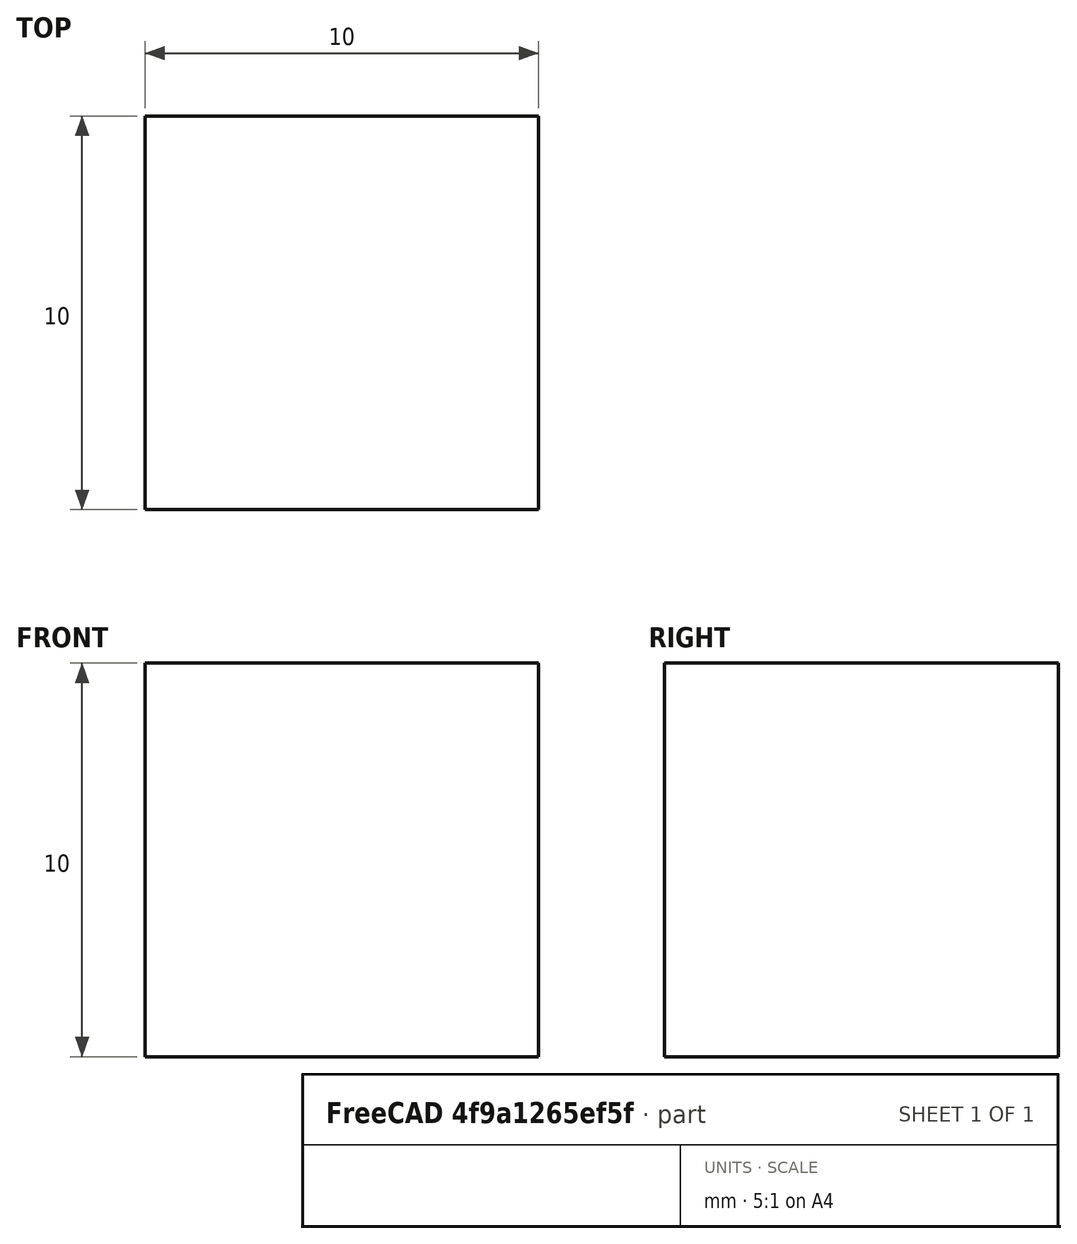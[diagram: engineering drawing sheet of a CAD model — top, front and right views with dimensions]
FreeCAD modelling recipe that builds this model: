
FCSTD DOCUMENT  (FreeCAD 0.21R33694 (Git))
Label: Block_Disp_Control_Example
License: All rights reserved
LicenseURL: http://en.wikipedia.org/wiki/All_rights_reserved
objects: Fem::ConstraintDisplacement×4, Fem::FemMeshObjectPython×2, Part::Box×1, Fem::FemSolverObjectPython×1, App::MaterialObjectPython×1, Fem::FemResultObjectPython×1, Fem::FemAnalysis×1
note: 1 computed B-rep shape members (.brp) not serialized (recipe doc carries the construction recipe, not evaluated geometry)

FEATURE [Part::Box] Box  label="Cube"
  AttacherType = Attacher::AttachEngine3D
  Height = 10
  Length = 10
  MapMode = 0
  Width = 10
FEATURE [Fem::FemSolverObjectPython] SolverCcxTools  # WARN: FeaturePython — macro-defined, semantics opaque (R4)
  AnalysisType = 0
  BeamShellResultOutput3D = false
  BucklingFactors = 1
  EigenmodeHighLimit = 1000000
  EigenmodeLowLimit = 0
  EigenmodesCount = 10
  GeometricalNonlinearity = 0
  IterationsControlParameterCutb = 0.25,0.5,0.75,0.85,,,1.5,
  IterationsControlParameterIter = 4,8,9,200,10,400,,200,,
  IterationsControlParameterTimeUse = false
  IterationsThermoMechMaximum = 2000
  IterationsUserDefinedIncrementations = false
  IterationsUserDefinedTimeStepLength = false
  MaterialNonlinearity = 0
  MatrixSolverType = 0
  SplitInputWriter = false
  ThermoMechSteadyState = true
  TimeEnd = 1
  TimeInitialStep = 0.01
FEATURE [App::MaterialObjectPython] MaterialSolid  # WARN: FeaturePython — macro-defined, semantics opaque (R4)
  Category = 0
FEATURE [Fem::FemMeshObjectPython] FEMMeshGmsh  # WARN: FeaturePython — macro-defined, semantics opaque (R4)
  Algorithm2D = 0
  Algorithm3D = 0
  CharacteristicLengthMax = 0
  CharacteristicLengthMin = 10
  CoherenceMesh = true
  ElementDimension = 0
  ElementOrder = 1
  GeometryTolerance = 1e-06
  GroupsOfNodes = false
  HighOrderOptimize = 0
  MeshSizeFromCurvature = 12
  OptimizeNetgen = false
  OptimizeStd = true
  Part = -> Box
  RecombinationAlgorithm = 0
  Recombine3DAll = false
  RecombineAll = false
  SecondOrderLinear = false
FEATURE [Fem::ConstraintDisplacement] ConstraintDisplacement
  NormalDirection = (0,0,-1)
  References = -> [Box]
  Scale = 1
  hasXFormula = false
  hasYFormula = false
  hasZFormula = false
  rotxFix = false
  rotxFree = true
  rotyFix = false
  rotyFree = true
  rotzFix = false
  rotzFree = true
  useFlowSurfaceForce = false
  xDisplacement = 0
  xFix = false
  xFree = true
  xRotation = 0
  yDisplacement = 0
  yFix = false
  yFree = true
  yRotation = 0
  zDisplacement = 0
  zFix = false
  zFree = false
  zRotation = 0
FEATURE [Fem::ConstraintDisplacement] ConstraintDisplacement001
  NormalDirection = (-1,0,0)
  References = -> [Box]
  Scale = 1
  hasXFormula = false
  hasYFormula = false
  hasZFormula = false
  rotxFix = false
  rotxFree = true
  rotyFix = false
  rotyFree = true
  rotzFix = false
  rotzFree = true
  useFlowSurfaceForce = false
  xDisplacement = 0
  xFix = false
  xFree = false
  xRotation = 0
  yDisplacement = 0
  yFix = false
  yFree = true
  yRotation = 0
  zDisplacement = 0
  zFix = false
  zFree = true
  zRotation = 0
FEATURE [Fem::ConstraintDisplacement] ConstraintDisplacement002
  NormalDirection = (0,1,0)
  References = -> [Box]
  Scale = 1
  hasXFormula = false
  hasYFormula = false
  hasZFormula = false
  rotxFix = false
  rotxFree = true
  rotyFix = false
  rotyFree = true
  rotzFix = false
  rotzFree = true
  useFlowSurfaceForce = false
  xDisplacement = 0
  xFix = false
  xFree = true
  xRotation = 0
  yDisplacement = 0
  yFix = false
  yFree = false
  yRotation = 0
  zDisplacement = 0
  zFix = false
  zFree = true
  zRotation = 0
FEATURE [Fem::ConstraintDisplacement] ConstraintDisplacement003
  NormalDirection = (0,0,1)
  References = -> [Box]
  Scale = 1
  hasXFormula = false
  hasYFormula = false
  hasZFormula = false
  rotxFix = false
  rotxFree = true
  rotyFix = false
  rotyFree = true
  rotzFix = false
  rotzFree = true
  useFlowSurfaceForce = false
  xDisplacement = 0
  xFix = false
  xFree = true
  xRotation = 0
  yDisplacement = 0
  yFix = false
  yFree = true
  yRotation = 0
  zDisplacement = -0.1
  zFix = false
  zFree = false
  zRotation = 0
FEATURE [Fem::FemMeshObjectPython] Result_Mesh_Volume  # WARN: FeaturePython — macro-defined, semantics opaque (R4)
FEATURE [Fem::FemResultObjectPython] ResultMechanical  # WARN: FeaturePython — macro-defined, semantics opaque (R4)
  Eigenmode = 0
  EigenmodeFrequency = 0
  Mesh = -> Result_Mesh_Volume
  ResultType = Fem::ResultMechanical
  Time = 0
FEATURE [Fem::FemAnalysis] Analysis
  Group = -> [SolverCcxTools,MaterialSolid,FEMMeshGmsh,ConstraintDisplacement,ConstraintDisplacement001,ConstraintDisplacement002,ConstraintDisplacement003,ResultMechanical]
